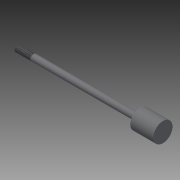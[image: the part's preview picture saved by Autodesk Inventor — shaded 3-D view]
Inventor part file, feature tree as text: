
AUTODESK INVENTOR PART (.ipt)
format: ipt  version: 2014 (Build 180170000, 170)  size: 125,952 bytes
history: native  units: in
note: dims shown in document units (in); Inventor stores cm internally (conversion verified against a paired STEP export)
features: other x49, revolve x3, sketch x3, thread x1
ambient origin geometry x8: Origin, YZ Plane, XZ Plane, XY Plane, X Axis, Y Axis, Z Axis, Center Point
bodies: Solid1 (feature_tree)
feature tree (56):
  revolve  "Revolution1"  [1 undecoded]
  thread  "Thread1"  [1 undecoded]
  revolve  "Revolution2"  [1 undecoded]
  revolve  "Revolution3"  [1 undecoded]
  other  "h1_XY"
  other  "h1_YZ"
  other  "h1_ZX"
  other  "h1_X"
  other  "h1_Y"
  other  "h1_Z"
  other  "h1_Center"
  other  "h2_XY"
  other  "h2_YZ"
  other  "h2_ZX"
  other  "h2_X"
  other  "h2_Y"
  other  "h2_Z"
  other  "h2_Center"
  other  "k1_XY"
  other  "k1_YZ"
  other  "k1_ZX"
  other  "k1_X"
  other  "k1_Y"
  other  "k1_Z"
  other  "k1_Center"
  other  "k2_XY"
  other  "k2_YZ"
  other  "k2_ZX"
  other  "k2_X"
  other  "k2_Y"
  other  "k2_Z"
  other  "k2_Center"
  other  "start_XY"
  other  "start_YZ"
  other  "start_ZX"
  other  "start_X"
  other  "start_Y"
  other  "start_Z"
  other  "start_Center"
  other  "to_prc_XY"
  other  "to_prc_YZ"
  other  "to_prc_ZX"
  other  "to_prc_X"
  other  "to_prc_Y"
  other  "to_prc_Z"
  other  "to_prc_Center"
  other  "to_rod_guide_XY"
  other  "to_rod_guide_YZ"
  other  "to_rod_guide_ZX"
  other  "to_rod_guide_X"
  other  "to_rod_guide_Y"
  other  "to_rod_guide_Z"
  other  "to_rod_guide_Center"
  sketch  "Sketch_3"  dims[d0=360.0deg d1=0.49in d2=3.791in d3=360.0deg]
  sketch  "Sketch_17"
  sketch  "Sketch_12"  dims[d4=360.0deg]
note: 4 required parameter values undecoded (feature->parameter linkage not recoverable at this tier; creation-order binding heuristic only, values carry confidence <= 0.55)